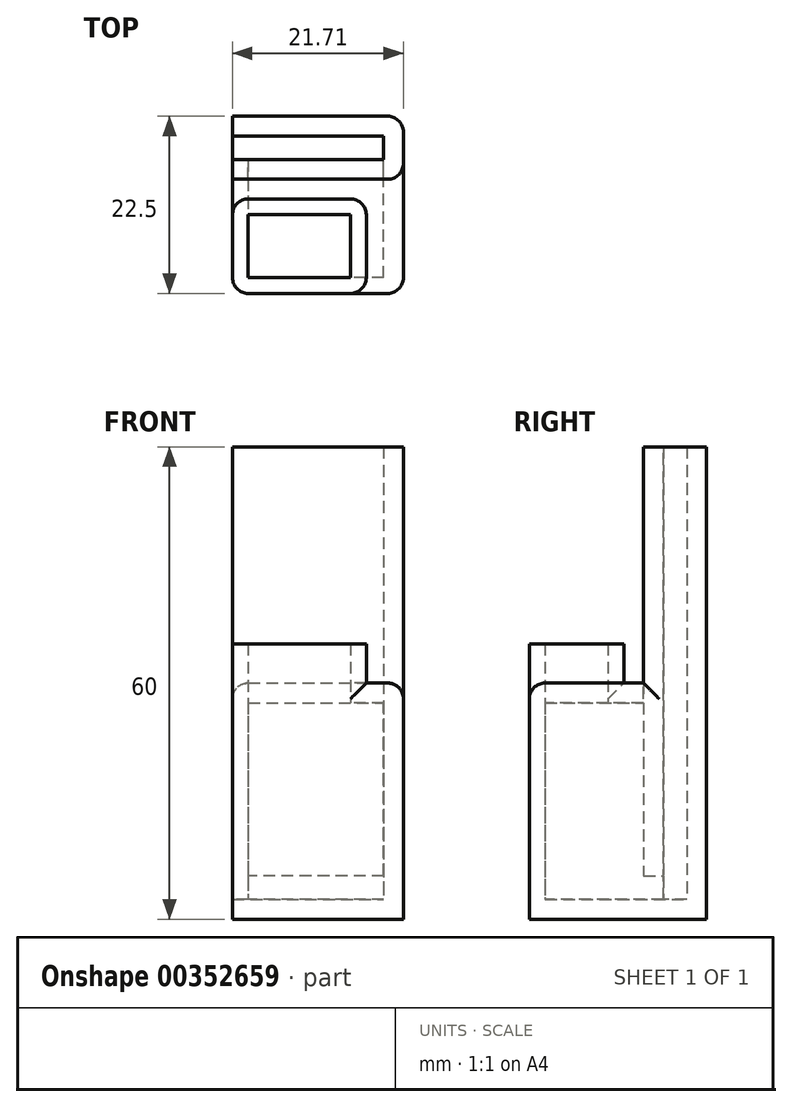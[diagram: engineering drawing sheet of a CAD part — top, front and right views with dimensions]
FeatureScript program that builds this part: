
annotation { "Feature Type Name" : "Feature", "Feature Type Description" : "" }
export const myFeature = defineFeature(function(context is Context, id is Id, definition is map)
    precondition{}
    {
        {
            var Q0;
            Q0=qCreatedBy(makeId("Top.planeOp"),FACE);
            var sketch = newSketch(context, id + "F0", { "sketchPlane" : qUnion([Q0])});
            skLineSegment(sketch, "E0.bottom", {"start": v(-8.5, 6) * mm, "end": v(8.5, 6) * mm});
            skLineSegment(sketch, "E0.top", {"start": v(-8.5, -6) * mm, "end": v(8.5, -6) * mm});
            skLineSegment(sketch, "E0.left", {"start": v(-8.5, 6) * mm, "end": v(-8.5, -6) * mm});
            skLineSegment(sketch, "E0.right", {"start": v(8.5, 6) * mm, "end": v(8.5, -6) * mm});
            skPoint(sketch, "E0.middle", {"position": v(0, 0) * mm});
            skLineSegment(sketch, "E1.bottom", {"start": v(-6.5, 4) * mm, "end": v(6.5, 4) * mm});
            skLineSegment(sketch, "E1.top", {"start": v(-6.5, -4) * mm, "end": v(6.5, -4) * mm});
            skLineSegment(sketch, "E1.left", {"start": v(-6.5, 4) * mm, "end": v(-6.5, -4) * mm});
            skLineSegment(sketch, "E1.right", {"start": v(6.5, 4) * mm, "end": v(6.5, -4) * mm});
            skSolve(sketch);
        }
        {
            var Q0;
            Q0=makeQuery(id+"F0.imprint","IMPRINT",FACE,{"disambiguationData":[TD([[makeQuery(id+"F0.imprint","IMPRINT",EDGE,{"derivedFrom":sQuery(id+"F0.wireOp",EDGE,"E0.bottom")}),-1.0]])]});
            extrude(context, id + "F1", {"entities" : qUnion([Q0]), "depth" : 5 * mm});
        }
        {
            var Q0;
            Q0=makeQuery(id+"F1.opExtrude","SWEPT_EDGE",EDGE,{"disambiguationData":[OSD([sQuery(id+"F0.wireOp",EDGE,"E0.top"),sQuery(id+"F0.wireOp",EDGE,"E0.left")])]});
            var Q1;
            Q1=makeQuery(id+"F1.opExtrude","SWEPT_EDGE",EDGE,{"disambiguationData":[OSD([sQuery(id+"F0.wireOp",EDGE,"E0.bottom"),sQuery(id+"F0.wireOp",EDGE,"E0.left")])]});
            var Q2;
            Q2=makeQuery(id+"F1.opExtrude","SWEPT_EDGE",EDGE,{"disambiguationData":[OSD([sQuery(id+"F0.wireOp",EDGE,"E0.bottom"),sQuery(id+"F0.wireOp",EDGE,"E0.right")])]});
            var Q3;
            Q3=makeQuery(id+"F1.opExtrude","SWEPT_EDGE",EDGE,{"disambiguationData":[OSD([sQuery(id+"F0.wireOp",EDGE,"E0.top"),sQuery(id+"F0.wireOp",EDGE,"E0.right")])]});
            fillet(context, id + "F2", {"entities" : qUnion([Q0, Q1, Q2, Q3]), "radius" : 2 * mm, "tangentPropagation" : true, "allowEdgeOverflow" : false});
        }
        {
            var Q0;
            Q0=makeQuery(id+"F1.opExtrude","CAP_FACE",FACE,{"disambiguationData":[OSD([sQuery(id+"F0.wireOp",EDGE,"E0.bottom"),sQuery(id+"F0.wireOp",EDGE,"E0.top"),sQuery(id+"F0.wireOp",EDGE,"E0.left"),sQuery(id+"F0.wireOp",EDGE,"E0.right"),sQuery(id+"F0.wireOp",EDGE,"E1.bottom"),sQuery(id+"F0.wireOp",EDGE,"E1.top"),sQuery(id+"F0.wireOp",EDGE,"E1.left"),sQuery(id+"F0.wireOp",EDGE,"E1.right")])],"isStart":true});
            var sketch = newSketch(context, id + "F3", { "sketchPlane" : qUnion([Q0])});
            skLineSegment(sketch, "E2.bottom", {"start": v(-8.5, 6) * mm, "end": v(13.21, 6) * mm});
            skLineSegment(sketch, "E2.top", {"start": v(-8.5, -11) * mm, "end": v(13.21, -11) * mm});
            skLineSegment(sketch, "E2.left", {"start": v(-8.5, 6) * mm, "end": v(-8.5, -11) * mm});
            skLineSegment(sketch, "E2.right", {"start": v(13.21, 6) * mm, "end": v(13.21, -11) * mm});
            skSolve(sketch);
        }
        {
            var Q0;
            {var subQ7=sQuery(id+"F3.wireOp",EDGE,"E2.top");Q0=makeQuery(id+"F3.imprint","IMPRINT",FACE,{"disambiguationData":[TD([[makeQuery(id+"F3.imprint","IMPRINT",EDGE,{"derivedFrom":subQ7}),1.0]])]});}
            var Q1;
            {var subQ3=sQuery(id+"F0.wireOp",EDGE,"E1.bottom");Q1=makeQuery(id+"F3.imprint","IMPRINT",FACE,{"disambiguationData":[TD([[makeQuery(id+"F3.imprint","IMPRINT",EDGE,{"derivedFrom":makeQuery(id+"F1.opExtrude","CAP_EDGE",EDGE,{"disambiguationData":[OSD([subQ3])],"isStart":true})}),-1.0]])]});}
            var Q2;
            Q2=makeQuery(id+"F3.imprint","IMPRINT",FACE,{"disambiguationData":[TD([[makeQuery(id+"F3.imprint","IMPRINT",EDGE,{"derivedFrom":makeQuery(id+"F1.opExtrude","CAP_EDGE",EDGE,{"disambiguationData":[OSD([sQuery(id+"F0.wireOp",EDGE,"E1.bottom")])],"isStart":true})}),1.0]])]});
            var Q3;
            Q3=makeQuery(id+"F3.imprint","IMPRINT",FACE,{"disambiguationData":[TD([[makeQuery(id+"F3.imprint","IMPRINT",EDGE,{"derivedFrom":sQuery(id+"F3.wireOp",EDGE,"XFVzFaLy-jCke-ttnu-qnLA-e7C1jFiiQSO1")}),1.0]])]});
            var Q4;
            Q4=makeQuery(id+"F3.imprint","IMPRINT",FACE,{"disambiguationData":[TD([[makeQuery(id+"F3.imprint","IMPRINT",EDGE,{"derivedFrom":sQuery(id+"F3.wireOp",EDGE,"seK892uO-QLs4-fr9K-BQBU-UyP4FAETu3PE")}),1.0]])]});
            extrude(context, id + "F4", {"entities" : qUnion([Q0, Q1, Q2, Q3, Q4]), "operationType" : NewBodyOperationType.ADD, "depth" : 30 * mm});
        }
        {
            var Q0;
            {var subQ0=sQuery(id+"F0.wireOp",EDGE,"E1.bottom");var subQ1=sQuery(id+"F0.wireOp",EDGE,"E1.top");var subQ2=sQuery(id+"F0.wireOp",EDGE,"E1.left");var subQ3=sQuery(id+"F0.wireOp",EDGE,"E1.right");Q0=makeQuery(id+"F4.boolean.opBoolean","SPLIT",FACE,{"disambiguationData":[TD([makeQuery(id+"F1.opExtrude","SWEPT_FACE",FACE,{"disambiguationData":[OSD([subQ0])]})])],"derivedFrom":makeQuery(id+"F4.opExtrude","CAP_FACE",FACE,{"disambiguationData":[OSD([sQuery(id+"F0.wireOp",EDGE,"E0.bottom"),sQuery(id+"F0.wireOp",EDGE,"E0.top"),sQuery(id+"F0.wireOp",EDGE,"E0.left"),sQuery(id+"F0.wireOp",EDGE,"E0.right"),subQ0,subQ1,subQ2,subQ3,sQuery(id+"F3.wireOp",EDGE,"E2.bottom"),sQuery(id+"F3.wireOp",EDGE,"E2.top"),sQuery(id+"F3.wireOp",EDGE,"E2.left"),sQuery(id+"F3.wireOp",EDGE,"E2.right")])],"isStart":true})});}
            shell(context, id + "F5", {"entities" : qUnion([Q0]), "thickness" : 2.5 * mm});
        }
        {
            var Q0;
            {var subQ0=sQuery(id+"F0.wireOp",EDGE,"E1.bottom");var subQ1=sQuery(id+"F0.wireOp",EDGE,"E1.top");var subQ2=sQuery(id+"F0.wireOp",EDGE,"E1.left");var subQ3=sQuery(id+"F0.wireOp",EDGE,"E1.right");Q0=makeQuery(id+"F4.boolean.opBoolean","SPLIT",FACE,{"disambiguationData":[TD([makeQuery(id+"F1.opExtrude","SWEPT_FACE",FACE,{"disambiguationData":[OSD([subQ0])]})])],"derivedFrom":makeQuery(id+"F4.opExtrude","CAP_FACE",FACE,{"disambiguationData":[OSD([sQuery(id+"F0.wireOp",EDGE,"E0.bottom"),sQuery(id+"F0.wireOp",EDGE,"E0.top"),sQuery(id+"F0.wireOp",EDGE,"E0.left"),sQuery(id+"F0.wireOp",EDGE,"E0.right"),subQ0,subQ1,subQ2,subQ3,sQuery(id+"F3.wireOp",EDGE,"E2.bottom"),sQuery(id+"F3.wireOp",EDGE,"E2.top"),sQuery(id+"F3.wireOp",EDGE,"E2.left"),sQuery(id+"F3.wireOp",EDGE,"E2.right")])],"isStart":true})});}
            var Q1;
            {var subQ0=sQuery(id+"F3.wireOp",EDGE,"E2.left");var subQ1=sQuery(id+"F3.wireOp",EDGE,"E2.top");var subQ2=sQuery(id+"F0.wireOp",EDGE,"E0.right");var subQ3=sQuery(id+"F0.wireOp",EDGE,"E0.top");var subQ4=sQuery(id+"F0.wireOp",EDGE,"E0.bottom");var subQ5=sQuery(id+"F3.wireOp",EDGE,"E2.bottom");var subQ6=sQuery(id+"F0.wireOp",EDGE,"E0.left");var subQ7=sQuery(id+"F3.wireOp",EDGE,"E2.right");var subQ8=sQuery(id+"F0.wireOp",EDGE,"E1.right");var subQ9=sQuery(id+"F0.wireOp",EDGE,"E1.left");var subQ10=sQuery(id+"F0.wireOp",EDGE,"E1.top");var subQ11=sQuery(id+"F0.wireOp",EDGE,"E1.bottom");Q1=makeQuery(id+"F5.opShell","OFFSET_FACE",FACE,{"disambiguationData":[OSD([subQ4,subQ3,subQ6,subQ2,subQ11,subQ10,subQ9,subQ8,subQ5,subQ1,subQ0,subQ7]),TDD([makeQuery(id+"F4.boolean.opBoolean","SPLIT",FACE,{"disambiguationData":[TD([makeQuery(id+"F1.opExtrude","SWEPT_FACE",FACE,{"disambiguationData":[OSD([subQ4])]})])],"derivedFrom":makeQuery(id+"F4.opExtrude","CAP_FACE",FACE,{"disambiguationData":[OSD([subQ4,subQ3,subQ6,subQ2,subQ11,subQ10,subQ9,subQ8,subQ5,subQ1,subQ0,subQ7])],"isStart":true})})])]});}
            extrude(context, id + "F6", {"entities" : qUnion([Q0]), "operationType" : NewBodyOperationType.REMOVE, "endBound" : BoundingType.UP_TO_SURFACE, "oppositeDirection" : true, "endBoundEntityFace" : qUnion([Q1]), "depth" : 25 * mm});
        }
        {
            var Q0;
            Q0=makeQuery(id+"F5.opShell","OFFSET_FACE",FACE,{"disambiguationData":[OSD([sQuery(id+"F0.wireOp",EDGE,"E0.top"),sQuery(id+"F3.wireOp",EDGE,"E2.bottom")])]});
            var Q1;
            {var subQ0=sQuery(id+"F0.wireOp",EDGE,"E1.top");Q1=makeQuery(id+"F6.boolean.opBoolean","MERGE",FACE,{"derivedFrom":[makeQuery(id+"F1.opExtrude","SWEPT_FACE",FACE,{"disambiguationData":[OSD([subQ0])]}),makeQuery(id+"F6.opExtrude","SWEPT_FACE",FACE,{"disambiguationData":[OSD([subQ0])]})]});}
            extrude(context, id + "F7", {"entities" : qUnion([Q0]), "operationType" : NewBodyOperationType.REMOVE, "endBound" : BoundingType.UP_TO_SURFACE, "oppositeDirection" : true, "endBoundEntityFace" : qUnion([Q1]), "depth" : 25 * mm});
        }
        {
            var Q0;
            {var subQ0=sQuery(id+"F3.wireOp",EDGE,"E2.left");var subQ1=sQuery(id+"F0.wireOp",EDGE,"E0.left");Q0=makeQuery(id+"F7.boolean.opBoolean","MERGE",FACE,{"derivedFrom":[makeQuery(id+"F5.opShell","OFFSET_FACE",FACE,{"disambiguationData":[OSD([subQ1,subQ0])]}),makeQuery(id+"F7.opExtrude","SWEPT_FACE",FACE,{"disambiguationData":[OSD([sQuery(id+"F0.wireOp",EDGE,"E0.bottom"),sQuery(id+"F0.wireOp",EDGE,"E0.top"),subQ1,sQuery(id+"F0.wireOp",EDGE,"E0.right"),sQuery(id+"F0.wireOp",EDGE,"E1.bottom"),sQuery(id+"F0.wireOp",EDGE,"E1.top"),sQuery(id+"F0.wireOp",EDGE,"E1.left"),sQuery(id+"F0.wireOp",EDGE,"E1.right"),sQuery(id+"F3.wireOp",EDGE,"E2.bottom"),subQ0])]})]});}
            var Q1;
            {var subQ0=sQuery(id+"F0.wireOp",EDGE,"E1.left");Q1=makeQuery(id+"F6.boolean.opBoolean","MERGE",FACE,{"derivedFrom":[makeQuery(id+"F1.opExtrude","SWEPT_FACE",FACE,{"disambiguationData":[OSD([subQ0])]}),makeQuery(id+"F6.opExtrude","SWEPT_FACE",FACE,{"disambiguationData":[OSD([subQ0])]})]});}
            extrude(context, id + "F8", {"entities" : qUnion([Q0]), "operationType" : NewBodyOperationType.REMOVE, "endBound" : BoundingType.UP_TO_SURFACE, "oppositeDirection" : true, "endBoundEntityFace" : qUnion([Q1]), "depth" : 25 * mm});
        }
        {
            var Q0;
            Q0=makeQuery(id+"F4.opExtrude","SWEPT_FACE",FACE,{"disambiguationData":[OSD([sQuery(id+"F3.wireOp",EDGE,"E2.top")])]});
            var sketch = newSketch(context, id + "F9", { "sketchPlane" : qUnion([Q0])});
            skLineSegment(sketch, "E3.bottom", {"start": v(-10.71, -24.5) * mm, "end": v(6.5, -24.5) * mm});
            skLineSegment(sketch, "E3.top", {"start": v(-10.71, -27.5) * mm, "end": v(6.5, -27.5) * mm});
            skLineSegment(sketch, "E3.left", {"start": v(-10.71, -24.5) * mm, "end": v(-10.71, -27.5) * mm});
            skLineSegment(sketch, "E3.right", {"start": v(6.5, -24.5) * mm, "end": v(6.5, -27.5) * mm});
            skSolve(sketch);
        }
        {
            var Q0;
            Q0=makeQuery(id+"F9.imprint","IMPRINT",FACE,{"disambiguationData":[TD([[makeQuery(id+"F9.imprint","IMPRINT",EDGE,{"derivedFrom":sQuery(id+"F9.wireOp",EDGE,"E3.bottom")}),-1.0]])]});
            extrude(context, id + "F10", {"entities" : qUnion([Q0]), "operationType" : NewBodyOperationType.REMOVE, "endBound" : BoundingType.UP_TO_NEXT, "oppositeDirection" : true, "depth" : 25 * mm});
        }
        {
            var Q0;
            Q0=makeQuery(id+"F4.opExtrude","CAP_FACE",FACE,{"disambiguationData":[OSD([sQuery(id+"F0.wireOp",EDGE,"E0.bottom"),sQuery(id+"F0.wireOp",EDGE,"E0.top"),sQuery(id+"F0.wireOp",EDGE,"E0.left"),sQuery(id+"F0.wireOp",EDGE,"E0.right"),sQuery(id+"F0.wireOp",EDGE,"E1.bottom"),sQuery(id+"F0.wireOp",EDGE,"E1.top"),sQuery(id+"F0.wireOp",EDGE,"E1.left"),sQuery(id+"F0.wireOp",EDGE,"E1.right"),sQuery(id+"F3.wireOp",EDGE,"E2.bottom"),sQuery(id+"F3.wireOp",EDGE,"E2.top"),sQuery(id+"F3.wireOp",EDGE,"E2.left"),sQuery(id+"F3.wireOp",EDGE,"E2.right")])],"isStart":false});
            var sketch = newSketch(context, id + "F11", { "sketchPlane" : qUnion([Q0])});
            skLineSegment(sketch, "E4.bottom", {"start": v(-8.5, -11) * mm, "end": v(13.21, -11) * mm});
            skLineSegment(sketch, "E4.top", {"start": v(-8.5, -16.5) * mm, "end": v(13.21, -16.5) * mm});
            skLineSegment(sketch, "E4.left", {"start": v(-8.5, -11) * mm, "end": v(-8.5, -16.5) * mm});
            skLineSegment(sketch, "E4.right", {"start": v(13.21, -11) * mm, "end": v(13.21, -16.5) * mm});
            skLineSegment(sketch, "E5", {"start": v(10.71, -11) * mm, "end": v(10.71, -14) * mm});
            skLineSegment(sketch, "E6", {"start": v(10.71, -14) * mm, "end": v(-8.5, -14) * mm});
            skLineSegment(sketch, "E7", {"start": v(-8.5, -14) * mm, "end": v(-8.5, -11) * mm});
            skSolve(sketch);
        }
        {
            var Q0;
            Q0=makeQuery(id+"F11.imprint","IMPRINT",FACE,{"disambiguationData":[TD([[makeQuery(id+"F11.imprint","IMPRINT",EDGE,{"derivedFrom":sQuery(id+"F11.wireOp",EDGE,"E4.top")}),1.0]])]});
            var Q1;
            {var subQ0=sQuery(id+"F3.wireOp",EDGE,"E2.left");var subQ1=sQuery(id+"F3.wireOp",EDGE,"E2.top");var subQ2=sQuery(id+"F0.wireOp",EDGE,"E0.right");var subQ3=sQuery(id+"F0.wireOp",EDGE,"E0.top");var subQ4=sQuery(id+"F0.wireOp",EDGE,"E0.bottom");var subQ5=sQuery(id+"F3.wireOp",EDGE,"E2.bottom");var subQ6=sQuery(id+"F0.wireOp",EDGE,"E0.left");var subQ7=sQuery(id+"F3.wireOp",EDGE,"E2.right");Q1=makeQuery(id+"F4.boolean.opBoolean","SPLIT",FACE,{"disambiguationData":[TD([makeQuery(id+"F1.opExtrude","SWEPT_FACE",FACE,{"disambiguationData":[OSD([subQ4])]})])],"derivedFrom":makeQuery(id+"F4.opExtrude","CAP_FACE",FACE,{"disambiguationData":[OSD([subQ4,subQ3,subQ6,subQ2,sQuery(id+"F0.wireOp",EDGE,"E1.bottom"),sQuery(id+"F0.wireOp",EDGE,"E1.top"),sQuery(id+"F0.wireOp",EDGE,"E1.left"),sQuery(id+"F0.wireOp",EDGE,"E1.right"),subQ5,subQ1,subQ0,subQ7])],"isStart":true})});}
            extrude(context, id + "F12", {"entities" : qUnion([Q0]), "operationType" : NewBodyOperationType.ADD, "endBound" : BoundingType.UP_TO_SURFACE, "oppositeDirection" : true, "endBoundEntityFace" : qUnion([Q1]), "depth" : 25 * mm});
        }
        {
            var Q0;
            {var subQ2=sQuery(id+"F11.wireOp",EDGE,"E5");Q0=makeQuery(id+"F11.imprint","IMPRINT",FACE,{"disambiguationData":[TD([[makeQuery(id+"F11.imprint","IMPRINT",EDGE,{"derivedFrom":subQ2}),-1.0]])]});}
            var Q1;
            {var subQ0=sQuery(id+"F3.wireOp",EDGE,"E2.left");var subQ1=sQuery(id+"F3.wireOp",EDGE,"E2.bottom");var subQ2=sQuery(id+"F0.wireOp",EDGE,"E1.right");var subQ3=sQuery(id+"F0.wireOp",EDGE,"E1.left");var subQ4=sQuery(id+"F0.wireOp",EDGE,"E1.top");var subQ5=sQuery(id+"F0.wireOp",EDGE,"E1.bottom");var subQ6=sQuery(id+"F0.wireOp",EDGE,"E0.right");var subQ7=sQuery(id+"F0.wireOp",EDGE,"E0.left");var subQ8=sQuery(id+"F0.wireOp",EDGE,"E0.top");var subQ9=sQuery(id+"F0.wireOp",EDGE,"E0.bottom");var subQ10=sQuery(id+"F3.wireOp",EDGE,"E2.right");var subQ11=sQuery(id+"F3.wireOp",EDGE,"E2.top");Q1=makeQuery(id+"F10.boolean.opBoolean","MERGE",FACE,{"derivedFrom":[makeQuery(id+"F8.boolean.opBoolean","MERGE",FACE,{"derivedFrom":[makeQuery(id+"F7.boolean.opBoolean","MERGE",FACE,{"derivedFrom":[makeQuery(id+"F5.opShell","OFFSET_FACE",FACE,{"disambiguationData":[OSD([subQ9,subQ8,subQ7,subQ6,subQ5,subQ4,subQ3,subQ2,subQ1,subQ11,subQ0,subQ10]),TDD([makeQuery(id+"F4.opExtrude","CAP_FACE",FACE,{"disambiguationData":[OSD([subQ9,subQ8,subQ7,subQ6,subQ5,subQ4,subQ3,subQ2,subQ1,subQ11,subQ0,subQ10])],"isStart":false})])]}),makeQuery(id+"F7.opExtrude","SWEPT_FACE",FACE,{"disambiguationData":[OSD([subQ1])]})]}),makeQuery(id+"F8.opExtrude","SWEPT_FACE",FACE,{"disambiguationData":[OSD([subQ9,subQ8,subQ7,subQ6,subQ5,subQ4,subQ3,subQ2,subQ1,subQ0]),TDD([makeQuery(id+"F7.boolean.opBoolean","MERGE",EDGE,{"derivedFrom":[makeQuery(id+"F5.opShell","OFFSET_EDGE",EDGE,{"disambiguationData":[OSD([subQ0]),TDD([makeQuery(id+"F4.opExtrude","CAP_EDGE",EDGE,{"disambiguationData":[OSD([subQ0])],"isStart":false})])]}),makeQuery(id+"F7.opExtrude","SWEPT_EDGE",EDGE,{"disambiguationData":[OSD([subQ9,subQ8,subQ7,subQ6,subQ5,subQ4,subQ3,subQ2,subQ1,subQ0])]})]})])]})]}),makeQuery(id+"F10.opExtrude","SWEPT_FACE",FACE,{"disambiguationData":[OSD([sQuery(id+"F9.wireOp",EDGE,"E3.top")])]})]});}
            extrude(context, id + "F13", {"entities" : qUnion([Q0]), "operationType" : NewBodyOperationType.ADD, "endBound" : BoundingType.UP_TO_SURFACE, "oppositeDirection" : true, "endBoundEntityFace" : qUnion([Q1]), "depth" : 25 * mm});
        }
        {
            var Q0;
            {var subQ0=sQuery(id+"F3.wireOp",EDGE,"E2.right");var subQ1=sQuery(id+"F3.wireOp",EDGE,"E2.left");var subQ2=sQuery(id+"F3.wireOp",EDGE,"E2.top");var subQ3=sQuery(id+"F3.wireOp",EDGE,"E2.bottom");var subQ4=sQuery(id+"F0.wireOp",EDGE,"E1.right");var subQ5=sQuery(id+"F0.wireOp",EDGE,"E1.left");var subQ6=sQuery(id+"F0.wireOp",EDGE,"E1.top");var subQ7=sQuery(id+"F0.wireOp",EDGE,"E1.bottom");var subQ8=sQuery(id+"F0.wireOp",EDGE,"E0.right");var subQ9=sQuery(id+"F0.wireOp",EDGE,"E0.left");var subQ10=sQuery(id+"F0.wireOp",EDGE,"E0.top");var subQ11=sQuery(id+"F0.wireOp",EDGE,"E0.bottom");Q0=makeQuery(id+"F12.boolean.opBoolean","MERGE",FACE,{"derivedFrom":[makeQuery(id+"F4.boolean.opBoolean","SPLIT",FACE,{"disambiguationData":[TD([makeQuery(id+"F1.opExtrude","SWEPT_FACE",FACE,{"disambiguationData":[OSD([subQ11])]})])],"derivedFrom":makeQuery(id+"F4.opExtrude","CAP_FACE",FACE,{"disambiguationData":[OSD([subQ11,subQ10,subQ9,subQ8,subQ7,subQ6,subQ5,subQ4,subQ3,subQ2,subQ1,subQ0])],"isStart":true})}),makeQuery(id+"F12.opExtrude","CAP_FACE",FACE,{"disambiguationData":[OSD([subQ11,subQ10,subQ9,subQ8,subQ7,subQ6,subQ5,subQ4,subQ3,subQ2,subQ1,subQ0])],"isStart":false})]});}
            var sketch = newSketch(context, id + "F14", { "sketchPlane" : qUnion([Q0])});
            skLineSegment(sketch, "E8", {"start": v(-8.5, 8.5) * mm, "end": v(13.21, 8.5) * mm});
            skSolve(sketch);
        }
        {
            var Q0;
            {var subQ10=sQuery(id+"F14.wireOp",EDGE,"E8");Q0=makeQuery(id+"F14.imprint","IMPRINT",FACE,{"disambiguationData":[TD([[makeQuery(id+"F14.imprint","IMPRINT",EDGE,{"derivedFrom":subQ10}),1.0]])]});}
            extrude(context, id + "F15", {"entities" : qUnion([Q0]), "operationType" : NewBodyOperationType.ADD, "depth" : 30 * mm});
        }
        {
            var Q0;
            Q0=makeQuery(id+"F4.opExtrude","SWEPT_EDGE",EDGE,{"disambiguationData":[OSD([sQuery(id+"F3.wireOp",EDGE,"E2.bottom"),sQuery(id+"F3.wireOp",EDGE,"E2.right")])]});
            var Q1;
            Q1=makeQuery(id+"F15.opExtrude","SWEPT_EDGE",EDGE,{"disambiguationData":[OSD([sQuery(id+"F0.wireOp",EDGE,"E0.bottom"),sQuery(id+"F0.wireOp",EDGE,"E0.top"),sQuery(id+"F0.wireOp",EDGE,"E0.left"),sQuery(id+"F0.wireOp",EDGE,"E0.right"),sQuery(id+"F0.wireOp",EDGE,"E1.bottom"),sQuery(id+"F0.wireOp",EDGE,"E1.top"),sQuery(id+"F0.wireOp",EDGE,"E1.left"),sQuery(id+"F0.wireOp",EDGE,"E1.right"),sQuery(id+"F3.wireOp",EDGE,"E2.bottom"),sQuery(id+"F3.wireOp",EDGE,"E2.top"),sQuery(id+"F3.wireOp",EDGE,"E2.left"),sQuery(id+"F3.wireOp",EDGE,"E2.right"),sQuery(id+"F11.wireOp",EDGE,"E4.right"),sQuery(id+"F14.wireOp",EDGE,"E8")])]});
            var Q2;
            {var subQ0=sQuery(id+"F11.wireOp",EDGE,"E4.right");var subQ1=sQuery(id+"F11.wireOp",EDGE,"E4.top");Q2=makeQuery(id+"F15.boolean.opBoolean","MERGE",EDGE,{"derivedFrom":[makeQuery(id+"F12.opExtrude","SWEPT_EDGE",EDGE,{"disambiguationData":[OSD([subQ1,subQ0])]}),makeQuery(id+"F15.opExtrude","SWEPT_EDGE",EDGE,{"disambiguationData":[OSD([sQuery(id+"F0.wireOp",EDGE,"E0.bottom"),sQuery(id+"F0.wireOp",EDGE,"E0.top"),sQuery(id+"F0.wireOp",EDGE,"E0.left"),sQuery(id+"F0.wireOp",EDGE,"E0.right"),sQuery(id+"F0.wireOp",EDGE,"E1.bottom"),sQuery(id+"F0.wireOp",EDGE,"E1.top"),sQuery(id+"F0.wireOp",EDGE,"E1.left"),sQuery(id+"F0.wireOp",EDGE,"E1.right"),sQuery(id+"F3.wireOp",EDGE,"E2.bottom"),sQuery(id+"F3.wireOp",EDGE,"E2.top"),sQuery(id+"F3.wireOp",EDGE,"E2.left"),sQuery(id+"F3.wireOp",EDGE,"E2.right"),subQ1,subQ0])]})]});}
            var Q3;
            {var subQ0=sQuery(id+"F3.wireOp",EDGE,"E2.left");var subQ1=sQuery(id+"F3.wireOp",EDGE,"E2.top");var subQ2=sQuery(id+"F0.wireOp",EDGE,"E0.right");var subQ3=sQuery(id+"F0.wireOp",EDGE,"E0.top");var subQ4=sQuery(id+"F0.wireOp",EDGE,"E0.bottom");var subQ5=sQuery(id+"F3.wireOp",EDGE,"E2.bottom");var subQ6=sQuery(id+"F0.wireOp",EDGE,"E0.left");var subQ7=sQuery(id+"F3.wireOp",EDGE,"E2.right");Q3=makeQuery(id+"F12.boolean.opBoolean","MERGE",EDGE,{"derivedFrom":[makeQuery(id+"F4.opExtrude","CAP_EDGE",EDGE,{"disambiguationData":[OSD([subQ7])],"isStart":true}),makeQuery(id+"F12.opExtrude","TWEAK_EDGE",EDGE,{"derivedFrom":[makeQuery(id+"F4.boolean.opBoolean","SPLIT",FACE,{"disambiguationData":[TD([makeQuery(id+"F1.opExtrude","SWEPT_FACE",FACE,{"disambiguationData":[OSD([subQ4])]})])],"derivedFrom":makeQuery(id+"F4.opExtrude","CAP_FACE",FACE,{"disambiguationData":[OSD([subQ4,subQ3,subQ6,subQ2,sQuery(id+"F0.wireOp",EDGE,"E1.bottom"),sQuery(id+"F0.wireOp",EDGE,"E1.top"),sQuery(id+"F0.wireOp",EDGE,"E1.left"),sQuery(id+"F0.wireOp",EDGE,"E1.right"),subQ5,subQ1,subQ0,subQ7])],"isStart":true})}),makeQuery(id+"F11.imprint","IMPRINT",EDGE,{"derivedFrom":sQuery(id+"F11.wireOp",EDGE,"E4.right")})]})]});}
            var Q4;
            Q4=makeQuery(id+"F4.opExtrude","CAP_EDGE",EDGE,{"disambiguationData":[OSD([sQuery(id+"F3.wireOp",EDGE,"E2.bottom")])],"isStart":true});
            var Q5;
            Q5=makeQuery(id+"F4.opExtrude","CAP_EDGE",EDGE,{"disambiguationData":[OSD([sQuery(id+"F3.wireOp",EDGE,"E2.left")])],"isStart":true});
            fillet(context, id + "F16", {"entities" : qUnion([Q0, Q1, Q2, Q3, Q4, Q5]), "radius" : 2 * mm, "tangentPropagation" : true, "allowEdgeOverflow" : false});
        }
    });
